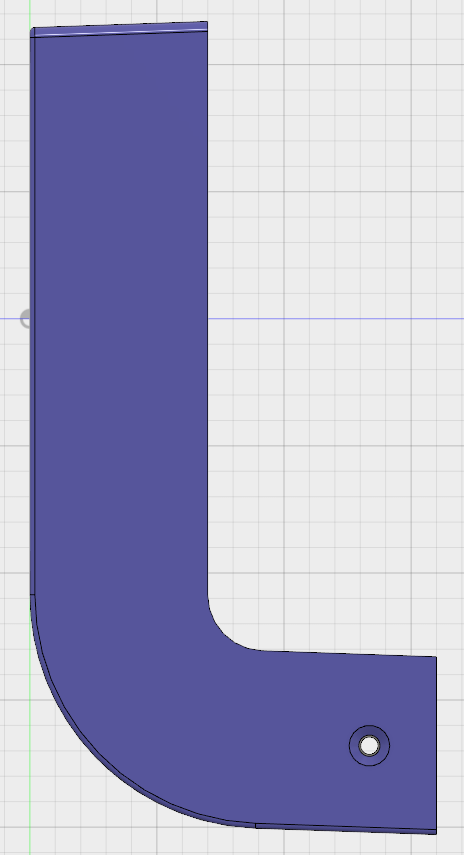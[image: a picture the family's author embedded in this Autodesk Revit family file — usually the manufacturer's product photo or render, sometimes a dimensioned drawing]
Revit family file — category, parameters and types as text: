
# Revit family: 0047932 Sylvania Lighting Fixture ST eco Surface Wall L-Shape IP54 570lm 830 BLK
name_source: partatom
category: Lighting Fixtures
revit_build: Autodesk Revit 2016 (Build: 20150220_1215(x64)
units: mm (PartAtom-declared; Revit-internal decimal feet)

## family parameters
Cut with Voids When Loaded = No
Host = Face
Light Source = Yes
OmniClass Number = 23.80.70.11.17
OmniClass Title = Specialized Lighting by Location or Use
Part Type = Normal
Room Calculation Point = No
Round Connector Dimension = Use Diameter
Shared = No

## types (1)
- 0047932 ST eco Surface Wall L-Shape IP54 570lm 830 BLK
    Apparent Load = 8 VA
    Assembly Code = D5020200
    Body Material = Aluminum_Sylvania_Velite_Black
    Catalog Number = 0047932 ST eco Surface Wall L-Shape IP54 570lm 830 BLK
    Color Filter = 16777215
    Default Elevation = 0 mm  [stored 0 ft]
    Description = A range of sleek and stylish Outdoor LED luminaires.Velite is perfect for lighting courtyards, gardens and exterior entrances.Design  meets IK05 requirements.Available in various shapes, sizes and colours of die cast aluminium luminaires.Range includes bollards and various wall mounted direct and direct/indirect luminaires.High efficient thermal design: ta -20 to +45oC.High performance: delivers up to 830 lm (luminaire lumen output), and up to 71lm/W (total system efficiency).Available in warm white (3,000K).Energy class: A++, A+, A.Lifetime: 30,000 hours life at 70% of the original output L70.
    Diffuser Material = Polycarbonate_Sylvania_Velite_Clear
    Dimming Lamp Color Temperature Shift = <None>
    Drive Current = 300mA
    Electrical Protection = CLASS I
    Energy Class = A++ A+ A
    Height = 80 mm  [stored 0.262467 ft]
    IK Rating = IK05
    IP Rating = IP54
    Lamp = LED
    Lamp Comments = Integrated LED
    Length = 90 mm  [stored 0.295276 ft]
    Life = 25 000h
    Manufacturer = Feilo Sylvania
    Model = ST eco Surface Wall L-Shape IP54 570lm 830 BLK
    Photometric Web File = 0047932.ies
    Product Page URL = http://www.sylvania-lighting.com
    Ta Rating = -20°C to +45°C
    Tilt Angle = 90.00°
    URL = http://www.sylvania-lighting.com
    Voltage = 240 V
    Voltage Comments = UNV (Universal Voltage; 230-240 Volt)
    Weight = 0.68 kg
    Width = 35 mm  [stored 0.114829 ft]

note: [stored X ft] marks values corroborated as IEEE doubles in the binary element streams (Revit-internal decimal feet)

## geometry (parser evidence)
native form markers: Blend x5, Sweep x4
no freeform markers — native parametric forms only
